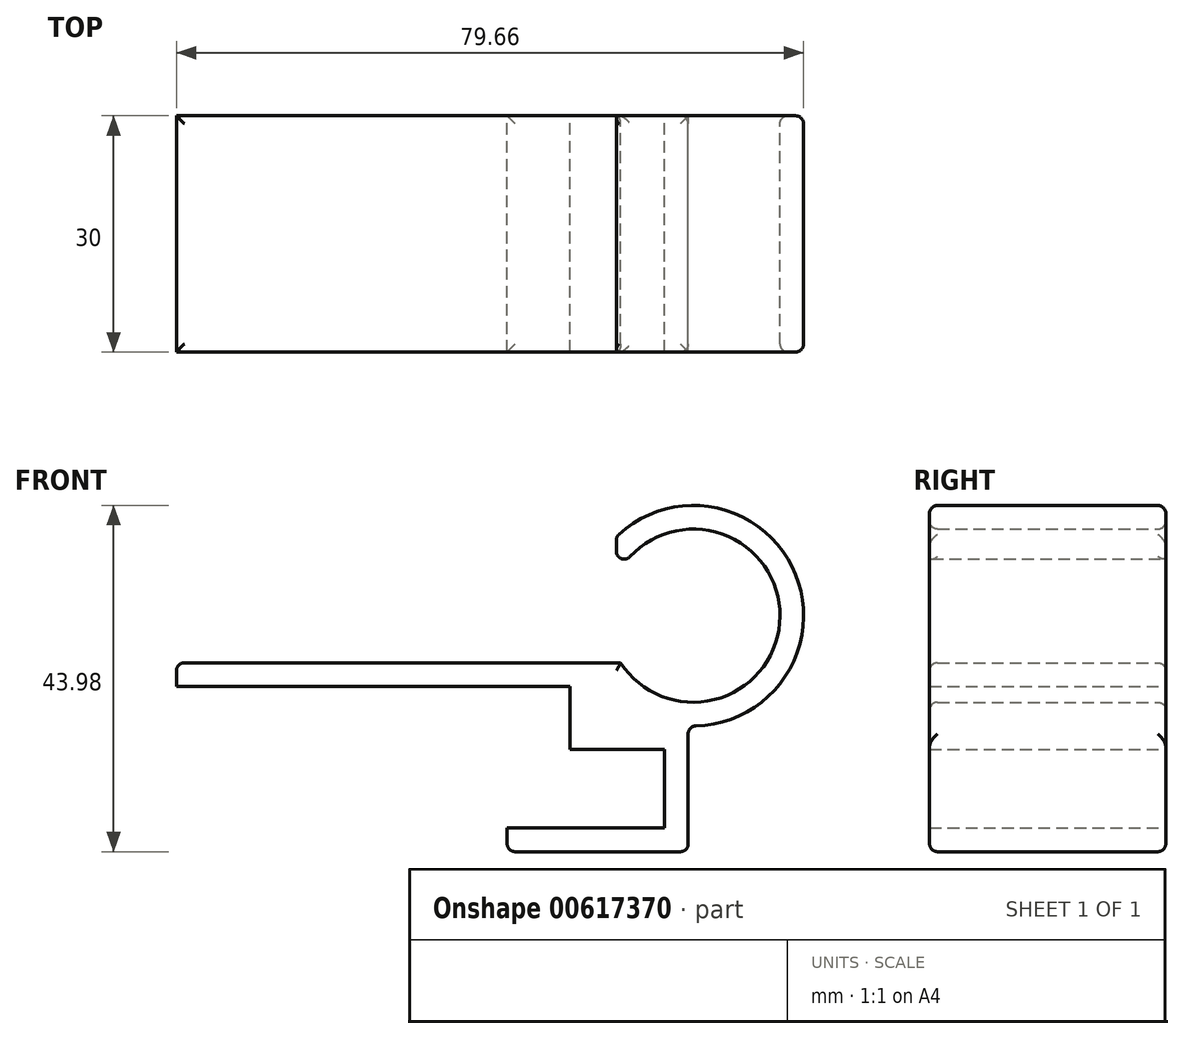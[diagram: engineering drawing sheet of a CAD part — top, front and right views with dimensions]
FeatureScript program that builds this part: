
annotation { "Feature Type Name" : "Feature", "Feature Type Description" : "" }
export const myFeature = defineFeature(function(context is Context, id is Id, definition is map)
    precondition{}
    {
        {
            var Q0;
            Q0=qCreatedBy(makeId("Front.planeOp"),FACE);
            var sketch = newSketch(context, id + "F0", { "sketchPlane" : qUnion([Q0])});
            skLineSegment(sketch, "E0.bottom", {"start": v(0, 0) * mm, "end": v(50, 0) * mm});
            skLineSegment(sketch, "E0.top", {"start": v(0, 3) * mm, "end": v(50, 3) * mm});
            skLineSegment(sketch, "E0.right", {"start": v(50, 0) * mm, "end": v(50, 3) * mm});
            skLineSegment(sketch, "E1.bottom", {"start": v(50, 3) * mm, "end": v(53, 3) * mm});
            skLineSegment(sketch, "E1.top", {"start": v(50, -8) * mm, "end": v(53, -8) * mm});
            skLineSegment(sketch, "E1.left", {"start": v(50, 3) * mm, "end": v(50, -8) * mm});
            skLineSegment(sketch, "E1.right", {"start": v(53, 3) * mm, "end": v(53, -8) * mm});
            skPoint(sketch, "E2", {"position": v(53, 0) * mm});
            skLineSegment(sketch, "E3.bottom", {"start": v(50, -8) * mm, "end": v(65, -8) * mm});
            skLineSegment(sketch, "E3.top", {"start": v(50, -5) * mm, "end": v(65, -5) * mm});
            skLineSegment(sketch, "E3.left", {"start": v(50, -8) * mm, "end": v(50, -5) * mm});
            skLineSegment(sketch, "E3.right", {"start": v(65, -8) * mm, "end": v(65, -5) * mm});
            skPoint(sketch, "E4", {"position": v(53, -5) * mm});
            skLineSegment(sketch, "E5.bottom", {"start": v(65, -5) * mm, "end": v(62, -5) * mm});
            skLineSegment(sketch, "E5.top", {"start": v(65, -18) * mm, "end": v(62, -18) * mm});
            skLineSegment(sketch, "E5.left", {"start": v(65, -5) * mm, "end": v(65, -18) * mm});
            skLineSegment(sketch, "E5.right", {"start": v(62, -5) * mm, "end": v(62, -18) * mm});
            skLineSegment(sketch, "E6.bottom", {"start": v(65, -18) * mm, "end": v(42, -18) * mm});
            skLineSegment(sketch, "E6.top", {"start": v(65, -21) * mm, "end": v(42, -21) * mm});
            skLineSegment(sketch, "E6.left", {"start": v(65, -18) * mm, "end": v(65, -21) * mm});
            skLineSegment(sketch, "E6.right", {"start": v(42, -18) * mm, "end": v(42, -21) * mm});
            skPoint(sketch, "E7", {"position": v(62, -8) * mm});
            skLineSegment(sketch, "E8", {"start": v(0, 3) * mm, "end": v(0, 0) * mm});
            skArc(sketch, "E9", {"start": v(56.43, 3) * mm, "mid": v(76.64, 9.54) * mm, "end": v(55.87, 14.02) * mm});
            skArc(sketch, "E10", {"start": v(53, 3) * mm, "mid": v(79.44, 6.5) * mm, "end": v(55.87, 19) * mm});
            skLineSegment(sketch, "E11.bottom", {"start": v(50, 3) * mm, "end": v(55.87, 3) * mm});
            skLineSegment(sketch, "E12.trimOffspring", {"start": v(55.87, 14.02) * mm, "end": v(55.87, 19) * mm});
            skLineSegment(sketch, "E13", {"start": v(55.87, 3) * mm, "end": v(56.43, 3) * mm});
            skSolve(sketch);
        }
        {
            var Q0;
            Q0=qSketchRegion(id+"F0",true);
            extrude(context, id + "F1", {"entities" : qUnion([Q0]), "depth" : 15 * mm, "hasSecondDirection" : true, "secondDirectionOppositeDirection" : true, "secondDirectionDepth" : 15 * mm, "offsetDistance" : 25 * mm});
        }
        {
            var Q0;
            Q0=makeQuery(id+"F1.opExtrude","SWEPT_EDGE",EDGE,{"disambiguationData":[OSD([sQuery(id+"F0.wireOp",EDGE,"E9"),sQuery(id+"F0.wireOp",EDGE,"E12.trimOffspring")])]});
            var Q1;
            Q1=makeQuery(id+"F1.opExtrude","SWEPT_EDGE",EDGE,{"disambiguationData":[OSD([sQuery(id+"F0.wireOp",EDGE,"E6.top"),sQuery(id+"F0.wireOp",EDGE,"E6.left")])]});
            var Q2;
            Q2=makeQuery(id+"F1.opExtrude","SWEPT_EDGE",EDGE,{"disambiguationData":[OSD([sQuery(id+"F0.wireOp",EDGE,"E0.top"),sQuery(id+"F0.wireOp",EDGE,"E8")])]});
            var Q3;
            Q3=makeQuery(id+"F1.opExtrude","CAP_EDGE",EDGE,{"disambiguationData":[OSD([sQuery(id+"F0.wireOp",EDGE,"E10")])],"isStart":false});
            var Q4;
            Q4=makeQuery(id+"F1.opExtrude","SWEPT_FACE",FACE,{"disambiguationData":[OSD([sQuery(id+"F0.wireOp",EDGE,"E10")])]});
            var Q5;
            Q5=makeQuery(id+"F1.opExtrude","CAP_EDGE",EDGE,{"disambiguationData":[OSD([sQuery(id+"F0.wireOp",EDGE,"E0.top"),sQuery(id+"F0.wireOp",EDGE,"E11.bottom"),sQuery(id+"F0.wireOp",EDGE,"E13")])],"isStart":true});
            var Q6;
            Q6=makeQuery(id+"F1.opExtrude","CAP_EDGE",EDGE,{"disambiguationData":[OSD([sQuery(id+"F0.wireOp",EDGE,"E0.top"),sQuery(id+"F0.wireOp",EDGE,"E11.bottom"),sQuery(id+"F0.wireOp",EDGE,"E13")])],"isStart":false});
            var Q7;
            Q7=makeQuery(id+"F1.opExtrude","CAP_EDGE",EDGE,{"disambiguationData":[OSD([sQuery(id+"F0.wireOp",EDGE,"E9")])],"isStart":false});
            var Q8;
            Q8=makeQuery(id+"F1.opExtrude","CAP_EDGE",EDGE,{"disambiguationData":[OSD([sQuery(id+"F0.wireOp",EDGE,"E9")])],"isStart":true});
            var Q9;
            Q9=makeQuery(id+"F1.opExtrude","CAP_EDGE",EDGE,{"disambiguationData":[OSD([sQuery(id+"F0.wireOp",EDGE,"E6.top")])],"isStart":false});
            var Q10;
            Q10=makeQuery(id+"F1.opExtrude","CAP_EDGE",EDGE,{"disambiguationData":[OSD([sQuery(id+"F0.wireOp",EDGE,"E6.top")])],"isStart":true});
            var Q11;
            Q11=makeQuery(id+"F1.opExtrude","SWEPT_EDGE",EDGE,{"disambiguationData":[OSD([sQuery(id+"F0.wireOp",EDGE,"E6.top"),sQuery(id+"F0.wireOp",EDGE,"E6.right")])]});
            fillet(context, id + "F2", {"entities" : qUnion([Q0, Q1, Q2, Q3, Q4, Q5, Q6, Q7, Q8, Q9, Q10, Q11]), "radius" : 1 * mm, "tangentPropagation" : true, "allowEdgeOverflow" : false});
        }
    });
